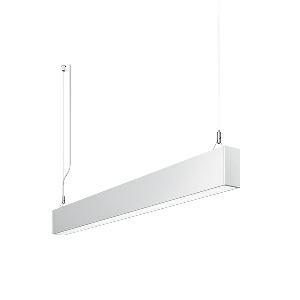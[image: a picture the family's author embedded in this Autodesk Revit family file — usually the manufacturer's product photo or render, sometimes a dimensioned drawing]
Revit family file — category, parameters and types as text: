
# Revit family: idoo_line_-_ilp_4000_vtl_d_00806452_c336
name_source: partatom
category: Lighting Fixtures
units: mm (PartAtom-declared; Revit-internal decimal feet)

## family parameters
Cut with Voids When Loaded = No
Host = Face
Light Source = No
Part Type = Normal
Room Calculation Point = No
Round Connector Dimension = Use Diameter
Shared = No

## types (1)
- IDOO.line - ILP 4000/VTL/D (1 x LED, 3850 lm, 2700-6500K)
    Apparent Load = 39 VA
    Approval mark = CE
    CIE Flux Codes = 66 91 98 40 100
    Color Rendering = 90-100
    Color Temperature = 2700-6500K
    Control Gear = Electronic ballast
    Default Elevation = 1800 mm
    Description = ILP 4000/VTL/D|Suspended luminaire|light source: LED|connected load: 220-240 V, 50/60 Hz|Power consumption: approx. 39 W|standby: approx. 0,25|luminous flux: 3850 lm|luminous efficacy: 98 lm/W|light distribution: Direct/indirect|direct ratio: approx. 40 %|colour temperature: Cold white, ca. 2700-6500 K|color rendering index (CRI): >= 90|chromaticity tolerance:  3 SDCM|System of protection: IP 40|technology: Continuously dimmable|luminaire body|material: Sectional aluminium|colour: White|lamp cover: Acrylic (PMMA), Clear|mains lead: 2.00 m With free stranded wires|Fastening: Steel cable 0.3 - 0.7 m|glare control: Prism aperture|luminance(L65): <= 2700 cd/m|unified glare rating(4H 8H): <=  16|special features: Specified values at approx. 4000 K, DALI Load 1x, External control required for Dali Device type 8, Flicker-free, Constant luminous flux between 2700 and 6500 K, Constant colour temperature over the whole dimming range, Suitable as emergency lighting|
    Frequency = 50 Hz
    Height = 110 mm
    Lamp = 1 x LED
    Lamp Light Flux = 3850 lm
    Lamp count = 1
    Length = 1414 mm
    Luminous efficacy = 99 lm/W
    Manufacturer = Waldmann
    ModVariant = No
    Model = 00806452
    Mounting Place = Ceiling
    Mounting Type = Pendant
    Number of Poles = 1
    OnlyDefault = Yes
    Power Factor = 1
    Product Name = IDOO.line - ILP 4000/VTL/D
    Product group = Suspended luminaire
    ProductGroupID = 9
    Protection Class = Protection class I
    Protection Degree = IP 40
    RLX_Detail_Level = 1
    RLX_Emergency_Light_Flux = 0 lm
    RLX_Emergency_Type = 0
    RLX_Emergency_Type_DB = No
    RlxData = <blob elided: 19877 chars, md5=8668ab83>
    Socket = socket
    Standby Power = 0 W
    System Light Flux = 3850 lm
    System Power = 39 W
    Type Comments = Product without accessories
    Type Image = 113291000-00692522.jpg
    URL = http://relux.com
    VarID = ---
    Voltage = 230 V
    Voltage Range = 220-240 V
    Weight = 0.00 kg
    Width = 60 mm  [stored 0.19685 ft]

note: [stored X ft] marks values corroborated as IEEE doubles in the binary element streams (Revit-internal decimal feet)

## geometry (parser evidence)
native form markers: Blend x4, Sweep x14
no freeform markers — native parametric forms only
